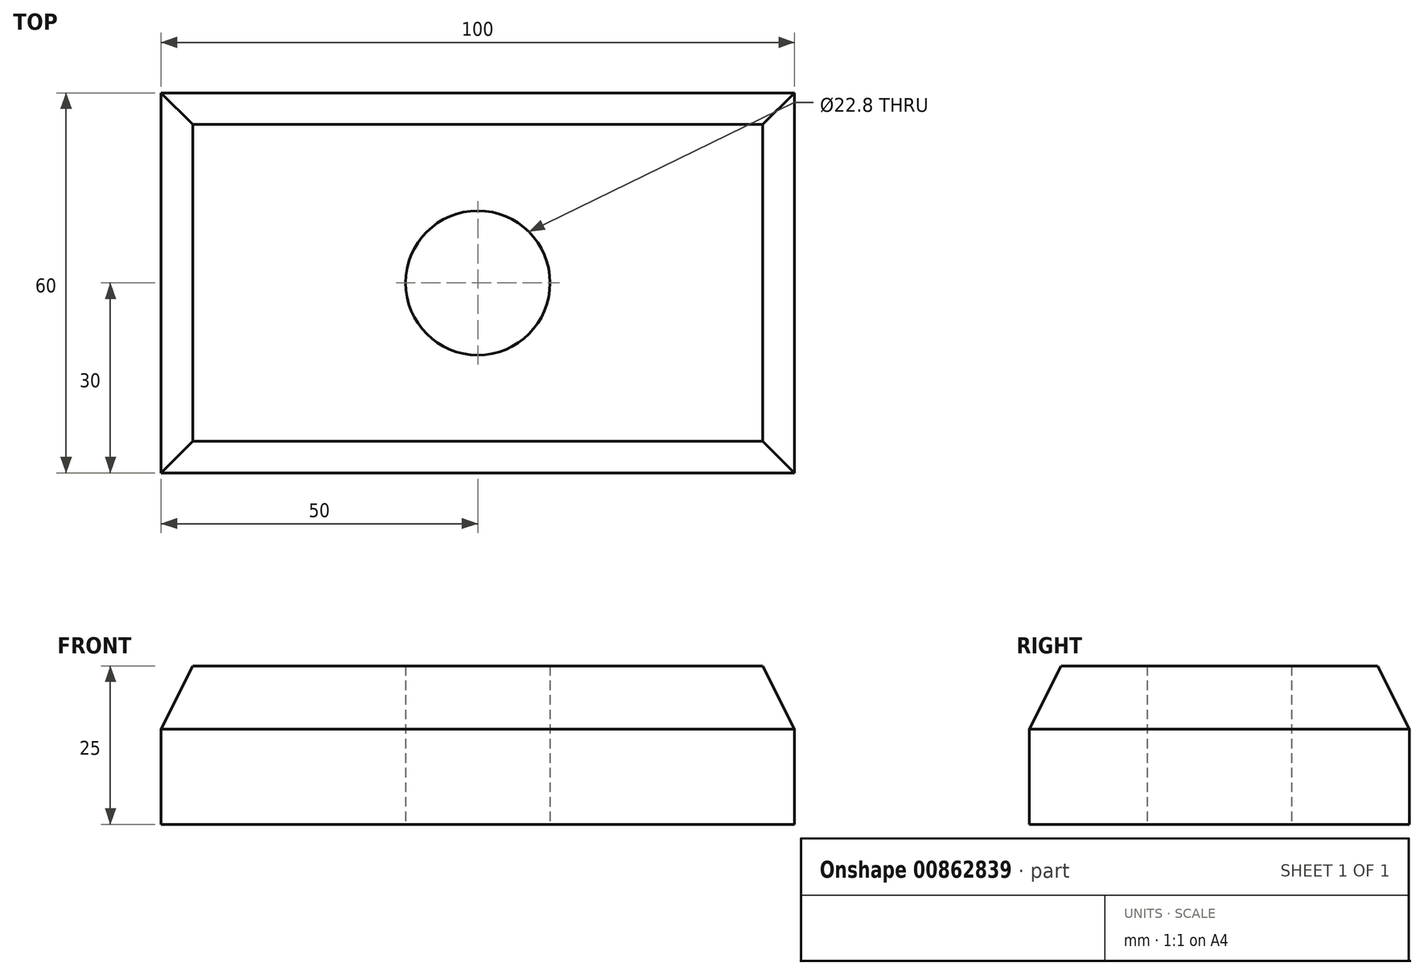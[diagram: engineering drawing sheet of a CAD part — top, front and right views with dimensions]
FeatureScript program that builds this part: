
annotation { "Feature Type Name" : "Feature", "Feature Type Description" : "" }
export const myFeature = defineFeature(function(context is Context, id is Id, definition is map)
    precondition{}
    {
        {
            var Q0;
            Q0=qCreatedBy(makeId("Top.planeOp"),FACE);
            var sketch = newSketch(context, id + "F0", { "sketchPlane" : qUnion([Q0])});
            skLineSegment(sketch, "E0.bottom", {"start": v(-50, 30) * mm, "end": v(50, 30) * mm});
            skLineSegment(sketch, "E0.top", {"start": v(-50, -30) * mm, "end": v(50, -30) * mm});
            skLineSegment(sketch, "E0.left", {"start": v(-50, 30) * mm, "end": v(-50, -30) * mm});
            skLineSegment(sketch, "E0.right", {"start": v(50, 30) * mm, "end": v(50, -30) * mm});
            skPoint(sketch, "E0.middle", {"position": v(0, 0) * mm});
            skCircle(sketch, "E1", {"center": v(0, 0) * mm, "radius": 11.4 * mm});
            skSolve(sketch);
        }
        {
            var Q0;
            Q0=makeQuery(id+"F0.imprint","IMPRINT",FACE,{"disambiguationData":[TD([[makeQuery(id+"F0.imprint","IMPRINT",EDGE,{"derivedFrom":sQuery(id+"F0.wireOp",EDGE,"E0.bottom")}),-1.0]])]});
            extrude(context, id + "F1", {"entities" : qUnion([Q0]), "depth" : 25 * mm, "offsetDistance" : 25 * mm});
        }
        {
            var Q0;
            Q0=makeQuery(id+"F1.opExtrude","CAP_EDGE",EDGE,{"disambiguationData":[OSD([sQuery(id+"F0.wireOp",EDGE,"E0.left")])],"isStart":false});
            var Q1;
            Q1=makeQuery(id+"F1.opExtrude","CAP_EDGE",EDGE,{"disambiguationData":[OSD([sQuery(id+"F0.wireOp",EDGE,"E0.top")])],"isStart":false});
            var Q2;
            Q2=makeQuery(id+"F1.opExtrude","CAP_EDGE",EDGE,{"disambiguationData":[OSD([sQuery(id+"F0.wireOp",EDGE,"E0.bottom")])],"isStart":false});
            var Q3;
            Q3=makeQuery(id+"F1.opExtrude","CAP_EDGE",EDGE,{"disambiguationData":[OSD([sQuery(id+"F0.wireOp",EDGE,"E0.right")])],"isStart":false});
            chamfer(context, id + "F2", {"entities" : qUnion([Q0, Q1, Q2, Q3]), "chamferType" : ChamferType.TWO_OFFSETS, "width1" : 5 * mm, "oppositeDirection" : false, "width2" : 10 * mm, "tangentPropagation" : true});
        }
    });
